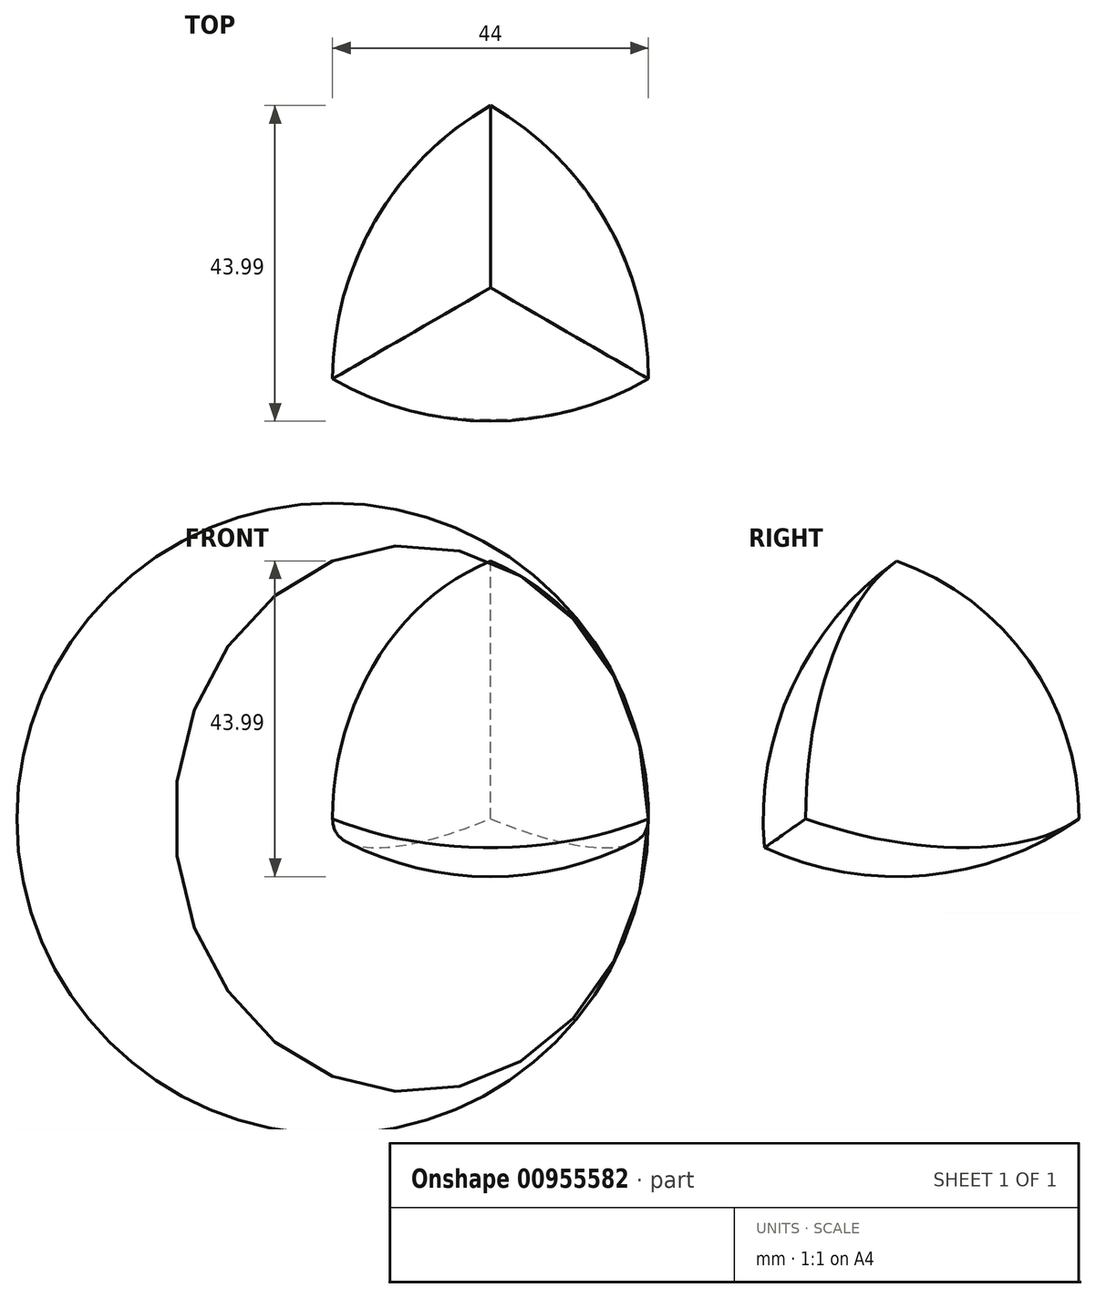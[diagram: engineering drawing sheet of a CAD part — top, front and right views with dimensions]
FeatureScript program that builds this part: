
annotation { "Feature Type Name" : "Feature", "Feature Type Description" : "" }
export const myFeature = defineFeature(function(context is Context, id is Id, definition is map)
    precondition{}
    {
        {
            var Q0;
            Q0=qCreatedBy(makeId("Top.planeOp"),FACE);
            var sketch = newSketch(context, id + "F0", { "sketchPlane" : qUnion([Q0])});
            skCircle(sketch, "E0.cCircle", {"center": v(0, 0) * mm, "radius": 25.4 * mm, "construction": true});
            skLineSegment(sketch, "E0.0", {"start": v(-44, 25.4) * mm, "end": v(44, 25.4) * mm, "construction": true});
            skLineSegment(sketch, "E0.1", {"start": v(44, 25.4) * mm, "end": v(0, -50.8) * mm, "construction": true});
            skLineSegment(sketch, "E0.2", {"start": v(0, -50.8) * mm, "end": v(-44, 25.4) * mm, "construction": true});
            skPoint(sketch, "E0.0.midPoint", {"position": v(0, 25.4) * mm});
            skLineSegment(sketch, "E1", {"start": v(0, 25.4) * mm, "end": v(0, 0) * mm, "construction": true});
            skLineSegment(sketch, "E2", {"start": v(22, -12.7) * mm, "end": v(0, 0) * mm, "construction": true});
            skLineSegment(sketch, "E3", {"start": v(-22, -12.7) * mm, "end": v(0, 0) * mm, "construction": true});
            skLineSegment(sketch, "E4", {"start": v(22, -12.7) * mm, "end": v(0, 25.4) * mm});
            skLineSegment(sketch, "E5", {"start": v(-22, -12.7) * mm, "end": v(0, 25.4) * mm});
            skLineSegment(sketch, "E6", {"start": v(-22, -12.7) * mm, "end": v(22, -12.7) * mm});
            skCircle(sketch, "E7", {"center": v(0, 25.4) * mm, "radius": 44 * mm});
            skCircle(sketch, "E8", {"center": v(22, -12.7) * mm, "radius": 44 * mm});
            skCircle(sketch, "E9", {"center": v(-22, -12.7) * mm, "radius": 44 * mm});
            skLineSegment(sketch, "E10", {"start": v(0, 25.4) * mm, "end": v(-22, 63.5) * mm});
            skLineSegment(sketch, "E11", {"start": v(-22, -12.7) * mm, "end": v(-44, -50.8) * mm});
            skLineSegment(sketch, "E12", {"start": v(22, -12.7) * mm, "end": v(66, -12.7) * mm});
            skSolve(sketch);
        }
        {
            var Q0;
            Q0=sQuery(id+"F0.wireOp",EDGE,"E2");
            cPlane(context, id + "F1", {"entities" : qUnion([Q0]), "cplaneType" : CPlaneType.LINE_ANGLE, "offset" : 25.4 * mm, "angle" : 0 * degree, "width" : 152.4 * mm, "height" : 152.4 * mm});
        }
        {
            var Q0;
            Q0=qCreatedBy(id+"F1.planeOp",FACE);
            var sketch = newSketch(context, id + "F2", { "sketchPlane" : qUnion([Q0])});
            skPoint(sketch, "E13", {"position": v(0, 35.92) * mm});
            skLineSegment(sketch, "E14", {"start": v(0, 35.92) * mm, "end": v(25.4, 0) * mm});
            skCircle(sketch, "E15", {"center": v(0, 35.92) * mm, "radius": 44 * mm});
            skLineSegment(sketch, "E16", {"start": v(0, 35.92) * mm, "end": v(-25.4, 71.84) * mm});
            skSolve(sketch);
        }
        {
            var Q0;
            {var subQ0=sQuery(id+"F2.wireOp",EDGE,"E14");Q0=makeQuery(id+"F2.imprint","IMPRINT",FACE,{"disambiguationData":[TD([[makeQuery(id+"F2.imprint","IMPRINT",EDGE,{"derivedFrom":subQ0}),-1.0]])]});}
            var Q1;
            Q1=sQuery(id+"F2.wireOp",EDGE,"E16");
            revolve(context, id + "F3", {"surfaceOperationType" : NewSurfaceOperationType.NEW, "entities" : qUnion([Q0]), "axis" : qUnion([Q1]), "revolveType" : RevolveType.FULL});
        }
        {
            var Q0;
            {var subQ0=sQuery(id+"F0.wireOp",EDGE,"E11");Q0=makeQuery(id+"F0.imprint","IMPRINT",FACE,{"disambiguationData":[TD([[makeQuery(id+"F0.imprint","IMPRINT",EDGE,{"derivedFrom":subQ0}),-1.0]])]});}
            var Q1;
            {var subQ1=sQuery(id+"F0.wireOp",EDGE,"E7");var subQ3=sQuery(id+"F0.wireOp",EDGE,"E9");var subQ4=makeQuery(id+"F0.imprint","INTERSECT",VERTEX,{"derivedFrom":[subQ1,subQ3]});Q1=makeQuery(id+"F0.imprint","IMPRINT",FACE,{"disambiguationData":[TD([[makeQuery(id+"F0.imprint","IMPRINT",EDGE,{"disambiguationData":[TD([[subQ4,-1.0]])],"derivedFrom":subQ1}),1.0]])]});}
            var Q2;
            {var subQ0=sQuery(id+"F0.wireOp",EDGE,"E5");Q2=makeQuery(id+"F0.imprint","IMPRINT",FACE,{"disambiguationData":[TD([[makeQuery(id+"F0.imprint","IMPRINT",EDGE,{"derivedFrom":subQ0}),1.0]])]});}
            var Q3;
            Q3=sQuery(id+"F0.wireOp",EDGE,"E11");
            revolve(context, id + "F4", {"operationType" : NewBodyOperationType.INTERSECT, "surfaceOperationType" : NewSurfaceOperationType.NEW, "entities" : qUnion([Q0, Q1, Q2]), "axis" : qUnion([Q3]), "revolveType" : RevolveType.FULL});
        }
        {
            var Q0;
            {var subQ0=sQuery(id+"F0.wireOp",EDGE,"E10");Q0=makeQuery(id+"F0.imprint","IMPRINT",FACE,{"disambiguationData":[TD([[makeQuery(id+"F0.imprint","IMPRINT",EDGE,{"derivedFrom":subQ0}),-1.0]])]});}
            var Q1;
            {var subQ1=sQuery(id+"F0.wireOp",EDGE,"E7");var subQ4=sQuery(id+"F0.wireOp",EDGE,"E8");var subQ5=makeQuery(id+"F0.imprint","INTERSECT",VERTEX,{"derivedFrom":[subQ1,subQ4]});Q1=makeQuery(id+"F0.imprint","IMPRINT",FACE,{"disambiguationData":[TD([[makeQuery(id+"F0.imprint","IMPRINT",EDGE,{"disambiguationData":[TD([[subQ5,1.0]])],"derivedFrom":subQ1}),1.0]])]});}
            var Q2;
            {var subQ0=sQuery(id+"F0.wireOp",EDGE,"E4");Q2=makeQuery(id+"F0.imprint","IMPRINT",FACE,{"disambiguationData":[TD([[makeQuery(id+"F0.imprint","IMPRINT",EDGE,{"derivedFrom":subQ0}),-1.0]])]});}
            var Q3;
            Q3=sQuery(id+"F0.wireOp",EDGE,"E10");
            revolve(context, id + "F5", {"operationType" : NewBodyOperationType.INTERSECT, "surfaceOperationType" : NewSurfaceOperationType.NEW, "entities" : qUnion([Q0, Q1, Q2]), "axis" : qUnion([Q3]), "revolveType" : RevolveType.FULL});
        }
        {
            var Q0;
            {var subQ0=sQuery(id+"F0.wireOp",EDGE,"E12");Q0=makeQuery(id+"F0.imprint","IMPRINT",FACE,{"disambiguationData":[TD([[makeQuery(id+"F0.imprint","IMPRINT",EDGE,{"derivedFrom":subQ0}),-1.0]])]});}
            var Q1;
            {var subQ0=sQuery(id+"F0.wireOp",EDGE,"E9");var subQ4=sQuery(id+"F0.wireOp",EDGE,"E8");var subQ6=makeQuery(id+"F0.imprint","INTERSECT",VERTEX,{"derivedFrom":[subQ4,subQ0]});Q1=makeQuery(id+"F0.imprint","IMPRINT",FACE,{"disambiguationData":[TD([[makeQuery(id+"F0.imprint","IMPRINT",EDGE,{"disambiguationData":[TD([[subQ6,1.0]])],"derivedFrom":subQ4}),1.0]])]});}
            var Q2;
            {var subQ0=sQuery(id+"F0.wireOp",EDGE,"E6");Q2=makeQuery(id+"F0.imprint","IMPRINT",FACE,{"disambiguationData":[TD([[makeQuery(id+"F0.imprint","IMPRINT",EDGE,{"derivedFrom":subQ0}),-1.0]])]});}
            var Q3;
            Q3=sQuery(id+"F0.wireOp",EDGE,"E12");
            revolve(context, id + "F6", {"operationType" : NewBodyOperationType.INTERSECT, "surfaceOperationType" : NewSurfaceOperationType.NEW, "entities" : qUnion([Q0, Q1, Q2]), "axis" : qUnion([Q3]), "revolveType" : RevolveType.FULL});
        }
    });
